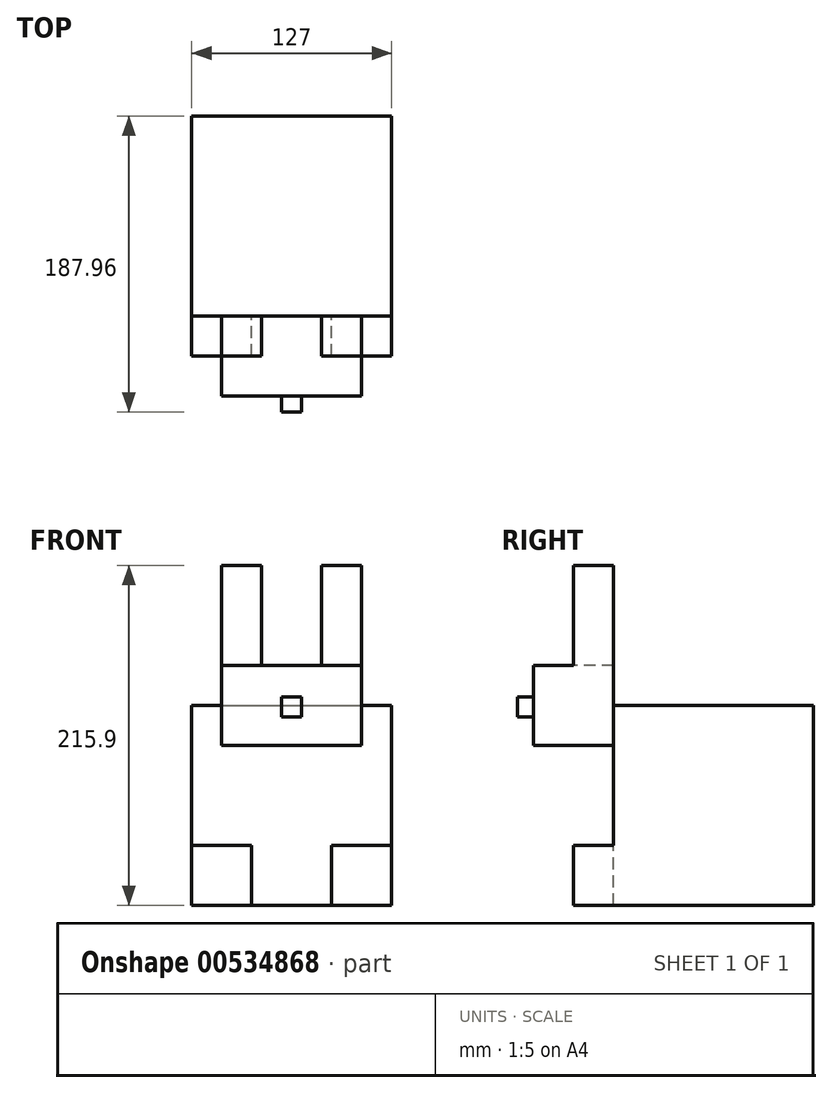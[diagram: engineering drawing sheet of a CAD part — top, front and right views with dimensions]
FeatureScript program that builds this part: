
annotation { "Feature Type Name" : "Feature", "Feature Type Description" : "" }
export const myFeature = defineFeature(function(context is Context, id is Id, definition is map)
    precondition{}
    {
        {
            var Q0;
            Q0=qCreatedBy(makeId("Front.planeOp"),FACE);
            var sketch = newSketch(context, id + "F0", { "sketchPlane" : qUnion([Q0])});
            skLineSegment(sketch, "E0.bottom", {"start": v(-63.5, 63.5) * mm, "end": v(63.5, 63.5) * mm});
            skLineSegment(sketch, "E0.top", {"start": v(-63.5, -63.5) * mm, "end": v(63.5, -63.5) * mm});
            skLineSegment(sketch, "E0.left", {"start": v(-63.5, 63.5) * mm, "end": v(-63.5, -63.5) * mm});
            skLineSegment(sketch, "E0.right", {"start": v(63.5, 63.5) * mm, "end": v(63.5, -63.5) * mm});
            skPoint(sketch, "E0.middle", {"position": v(0, 0) * mm});
            skSolve(sketch);
        }
        {
            var Q0;
            Q0=makeQuery(id+"F0.imprint","IMPRINT",FACE,{"disambiguationData":[TD([[makeQuery(id+"F0.imprint","IMPRINT",EDGE,{"derivedFrom":sQuery(id+"F0.wireOp",EDGE,"E0.bottom")}),-1.0]])]});
            extrude(context, id + "F1", {"entities" : qUnion([Q0]), "depth" : 127 * mm, "offsetDistance" : 25.4 * mm});
        }
        {
            var Q0;
            Q0=makeQuery(id+"F1.opExtrude","CAP_FACE",FACE,{"disambiguationData":[OSD([sQuery(id+"F0.wireOp",EDGE,"E0.bottom"),sQuery(id+"F0.wireOp",EDGE,"E0.top"),sQuery(id+"F0.wireOp",EDGE,"E0.left"),sQuery(id+"F0.wireOp",EDGE,"E0.right")])],"isStart":false});
            var sketch = newSketch(context, id + "F2", { "sketchPlane" : qUnion([Q0])});
            skLineSegment(sketch, "E1.bottom", {"start": v(-63.5, -63.5) * mm, "end": v(-25.4, -63.5) * mm});
            skLineSegment(sketch, "E1.top", {"start": v(-63.5, -25.4) * mm, "end": v(-25.4, -25.4) * mm});
            skLineSegment(sketch, "E1.left", {"start": v(-63.5, -63.5) * mm, "end": v(-63.5, -25.4) * mm});
            skLineSegment(sketch, "E1.right", {"start": v(-25.4, -63.5) * mm, "end": v(-25.4, -25.4) * mm});
            skLineSegment(sketch, "E2.bottom", {"start": v(63.5, -63.5) * mm, "end": v(25.4, -63.5) * mm});
            skLineSegment(sketch, "E2.top", {"start": v(63.5, -25.4) * mm, "end": v(25.4, -25.4) * mm});
            skLineSegment(sketch, "E2.left", {"start": v(63.5, -63.5) * mm, "end": v(63.5, -25.4) * mm});
            skLineSegment(sketch, "E2.right", {"start": v(25.4, -63.5) * mm, "end": v(25.4, -25.4) * mm});
            skLineSegment(sketch, "E3.bottom", {"start": v(-44.45, 88.9) * mm, "end": v(44.45, 88.9) * mm});
            skLineSegment(sketch, "E3.top", {"start": v(-44.45, 38.1) * mm, "end": v(44.45, 38.1) * mm});
            skLineSegment(sketch, "E3.left", {"start": v(-44.45, 88.9) * mm, "end": v(-44.45, 38.1) * mm});
            skLineSegment(sketch, "E3.right", {"start": v(44.45, 88.9) * mm, "end": v(44.45, 38.1) * mm});
            skPoint(sketch, "E3.middle", {"position": v(0, 63.5) * mm});
            skSolve(sketch);
        }
        {
            var Q0;
            Q0=makeQuery(id+"F2.imprint","IMPRINT",FACE,{"disambiguationData":[TD([[makeQuery(id+"F2.imprint","IMPRINT",EDGE,{"derivedFrom":sQuery(id+"F2.wireOp",EDGE,"E1.bottom")}),1.0]])]});
            var Q1;
            Q1=makeQuery(id+"F2.imprint","IMPRINT",FACE,{"disambiguationData":[TD([[makeQuery(id+"F2.imprint","IMPRINT",EDGE,{"derivedFrom":sQuery(id+"F2.wireOp",EDGE,"E2.bottom")}),1.0]])]});
            extrude(context, id + "F3", {"entities" : qUnion([Q0, Q1]), "operationType" : NewBodyOperationType.ADD, "depth" : 25.4 * mm, "offsetDistance" : 25.4 * mm});
        }
        {
            var Q0;
            Q0=makeQuery(id+"F1.opExtrude","CAP_FACE",FACE,{"disambiguationData":[OSD([sQuery(id+"F0.wireOp",EDGE,"E0.bottom"),sQuery(id+"F0.wireOp",EDGE,"E0.top"),sQuery(id+"F0.wireOp",EDGE,"E0.left"),sQuery(id+"F0.wireOp",EDGE,"E0.right")])],"isStart":false});
            var sketch = newSketch(context, id + "F4", { "sketchPlane" : qUnion([Q0])});
            skLineSegment(sketch, "E4.bottom", {"start": v(-44.45, 88.9) * mm, "end": v(44.45, 88.9) * mm});
            skLineSegment(sketch, "E4.top", {"start": v(-44.45, 38.1) * mm, "end": v(44.45, 38.1) * mm});
            skLineSegment(sketch, "E4.left", {"start": v(-44.45, 88.9) * mm, "end": v(-44.45, 38.1) * mm});
            skLineSegment(sketch, "E4.right", {"start": v(44.45, 88.9) * mm, "end": v(44.45, 38.1) * mm});
            skPoint(sketch, "E4.middle", {"position": v(0, 63.5) * mm});
            skSolve(sketch);
        }
        {
            var Q0;
            {var subQ0=sQuery(id+"F4.wireOp",EDGE,"E4.bottom");Q0=makeQuery(id+"F4.imprint","IMPRINT",FACE,{"disambiguationData":[TD([[makeQuery(id+"F4.imprint","IMPRINT",EDGE,{"derivedFrom":subQ0}),-1.0]])]});}
            var Q1;
            {var subQ0=sQuery(id+"F4.wireOp",EDGE,"E4.top");Q1=makeQuery(id+"F4.imprint","IMPRINT",FACE,{"disambiguationData":[TD([[makeQuery(id+"F4.imprint","IMPRINT",EDGE,{"derivedFrom":subQ0}),1.0]])]});}
            extrude(context, id + "F5", {"entities" : qUnion([Q0, Q1]), "operationType" : NewBodyOperationType.ADD, "depth" : 50.8 * mm, "offsetDistance" : 25.4 * mm});
        }
        {
            var Q0;
            Q0=makeQuery(id+"F5.opExtrude","SWEPT_FACE",FACE,{"disambiguationData":[OSD([sQuery(id+"F4.wireOp",EDGE,"E4.bottom")])]});
            var sketch = newSketch(context, id + "F6", { "sketchPlane" : qUnion([Q0])});
            skLineSegment(sketch, "E5.bottom", {"start": v(-44.45, -127) * mm, "end": v(-19.05, -127) * mm});
            skLineSegment(sketch, "E5.top", {"start": v(-44.45, -152.4) * mm, "end": v(-19.05, -152.4) * mm});
            skLineSegment(sketch, "E5.left", {"start": v(-44.45, -127) * mm, "end": v(-44.45, -152.4) * mm});
            skLineSegment(sketch, "E5.right", {"start": v(-19.05, -127) * mm, "end": v(-19.05, -152.4) * mm});
            skLineSegment(sketch, "E6.bottom", {"start": v(44.45, -127) * mm, "end": v(19.05, -127) * mm});
            skLineSegment(sketch, "E6.top", {"start": v(44.45, -152.4) * mm, "end": v(19.05, -152.4) * mm});
            skLineSegment(sketch, "E6.left", {"start": v(44.45, -127) * mm, "end": v(44.45, -152.4) * mm});
            skLineSegment(sketch, "E6.right", {"start": v(19.05, -127) * mm, "end": v(19.05, -152.4) * mm});
            skSolve(sketch);
        }
        {
            var Q0;
            Q0=makeQuery(id+"F6.imprint","IMPRINT",FACE,{"disambiguationData":[TD([[makeQuery(id+"F6.imprint","IMPRINT",EDGE,{"derivedFrom":sQuery(id+"F6.wireOp",EDGE,"E5.bottom")}),-1.0]])]});
            var Q1;
            Q1=makeQuery(id+"F6.imprint","IMPRINT",FACE,{"disambiguationData":[TD([[makeQuery(id+"F6.imprint","IMPRINT",EDGE,{"derivedFrom":sQuery(id+"F6.wireOp",EDGE,"E6.bottom")}),-1.0]])]});
            extrude(context, id + "F7", {"entities" : qUnion([Q0, Q1]), "operationType" : NewBodyOperationType.ADD, "depth" : 63.5 * mm, "offsetDistance" : 25.4 * mm});
        }
        {
            var Q0;
            Q0=makeQuery(id+"F5.opExtrude","CAP_FACE",FACE,{"disambiguationData":[OSD([sQuery(id+"F4.wireOp",EDGE,"E4.bottom"),sQuery(id+"F4.wireOp",EDGE,"E4.top"),sQuery(id+"F4.wireOp",EDGE,"E4.left"),sQuery(id+"F4.wireOp",EDGE,"E4.right")])],"isStart":false});
            var sketch = newSketch(context, id + "F8", { "sketchPlane" : qUnion([Q0])});
            skLineSegment(sketch, "E7.bottom", {"start": v(-6.35, 56.08) * mm, "end": v(6.35, 56.08) * mm});
            skLineSegment(sketch, "E7.top", {"start": v(-6.35, 68.78) * mm, "end": v(6.35, 68.78) * mm});
            skLineSegment(sketch, "E7.left", {"start": v(-6.35, 56.08) * mm, "end": v(-6.35, 68.78) * mm});
            skLineSegment(sketch, "E7.right", {"start": v(6.35, 56.08) * mm, "end": v(6.35, 68.78) * mm});
            skPoint(sketch, "E7.middle", {"position": v(0, 62.43) * mm});
            skSolve(sketch);
        }
        {
            var Q0;
            Q0=makeQuery(id+"F8.imprint","IMPRINT",FACE,{"disambiguationData":[TD([[makeQuery(id+"F8.imprint","IMPRINT",EDGE,{"derivedFrom":sQuery(id+"F8.wireOp",EDGE,"E7.bottom")}),1.0]])]});
            extrude(context, id + "F9", {"entities" : qUnion([Q0]), "operationType" : NewBodyOperationType.ADD, "depth" : 10.16 * mm, "offsetDistance" : 25.4 * mm});
        }
    });
